# Revit family: ITK Вентиляторная панель с выключателем и термостатом_32М
name_source: partatom
category: Электрооборудование
revit_build: Autodesk Revit 2016 (Build: 20160314_0715(x64)
units: mm (PartAtom-declared; Revit-internal decimal feet)

## family parameters
Всегда вертикально = Да
На основе рабочей плоскости = Нет
Общий = Нет
При загрузке вырезать с полостями = Нет
Размер круглого соединителя = Использовать диаметр
Тип детали = Другая панель
Точка расчета площади = Нет

## types (2) — shared parameters
ADSK_Единица измерения = шт
ADSK_Завод-изготовитель = IEK
ADSK_Классификация нагрузок = Прочее
ADSK_Количество фаз = 1
ADSK_Количество фаз числовое = 1
ADSK_Коэффициент мощности = 1
ADSK_Напряжение = 220 В
ADSK_Номинальная мощность = 1 Вт
ADSK_Полная мощность = 1 В·А
ADSK_Ток = 0 А
URL = http://www.itk-group.ru
Высота = 78 мм
Глубина = 171 мм
Изготовитель = ITK
Описание = Панели вентиляторные ITK серии ПВ предназначены для установки и использования в настенных шкафах серии LINEA W и сетевых шкафах LINEA N для организации принудительного охлаждения и вентиляции установленного в них активного (серверы, дисковые массивы, коммутаторы, ИБП и др.) оборудования и вывода из шкафа горячего воздуха.

Панели серии ПВ комплектуются выключателем со светоиндикацией, имеют два или три вентиляторных модуля и в зависимости от модели могут оснащаться биметаллическим термостатом (тип NO).
Диапазон регулировки температуры термостата: от 0 до 60°С.
Номинальное рабочее напряжение: 230В. Частота тока: 50Гц.
Минимальный срок службы: 50 тыс. часов.
Подача рабочего напряжения на вентиляторную панель осуществляется через встроенный разъем питания С14 10А/250В.

Внимание! Кабель электропитания для подключения к сети в комплект поставки не входит.

Вентиляторные панели устанавливаются в крыше шкафа на специально предусмотренное посадочное место и не занимают полезной высоты 19-дюймовых монтажных профилей.
Максимальное количество устанавливаемых в шкаф вентиляторных панелей в зависимости от его серии и габаритов:
LINEA W 600x450 мм - 1 шт.
LINEA W 600x600 мм - 2 шт.
LINEA N 600x600 мм - 2 шт.
LINEA N 600x800 мм - 3 шт.
LINEA N 600x1000 мм - 4 шт.
Совместимы со всеми 19-доймовыми шкафами и стойками ITK.
Обладают современным привлекательным дизайном и продуманной конструкцией.
Удобны в монтаже и эксплуатации.
Соответствие международным стандартам ISO9001, IEC 297, ISO/IEC 11801. 
Сертифицированы по ГОСТ Р.
Все аксессуары идут с крепежом.
Возможно исполнение в двух цветах: серый (RAL7035) и черный (RAL9005).
Всегда в наличии на складе.
Гарантия на все аксессуары до 2-х лет.
Совместимость = Linea N, W
Степень защиты = IP20
Ширина = 470 мм
zero-valued in all types: ADSK_Масса

## per-type parameters (varying)
| type | ADSK_Наименование | Материал |
| FM05-32M | ITK Вентиляторная панель с выключателем и термостатом, 3 модуля, черная | Окраска - RAL 9005 |
| FM35-32M | ITK Вентиляторная панель с выключателем и термостатом, 3 модуля,серая | Окраска - RAL 7035 |

note: column(s) folded — value = type name in every type: ADSK_Марка, ADSK_Наименование краткое
